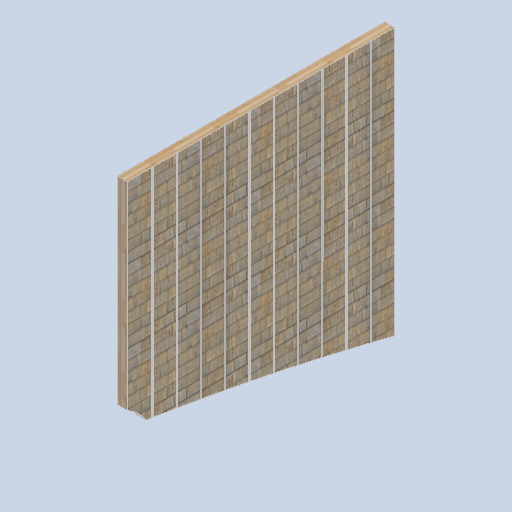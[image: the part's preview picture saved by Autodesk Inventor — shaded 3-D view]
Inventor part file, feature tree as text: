
AUTODESK INVENTOR PART (.ipt)
format: ipt  version: 2024.2 (Build 282272000, 272)  size: 508,928 bytes
history: native  units: mm
features: extrude x2, sketch x2
ambient origin geometry x8: Origin, YZ Plane, XZ Plane, XY Plane, X Axis, Y Axis, Z Axis, Center Point
bodies: Solid1 (feature_tree)
feature tree (4):
  extrude  "Extrusion1"  Depth=350.0mm
  extrude  "Extrusion2"  Depth=20.0mm
  sketch  "Sketch1"  dims[d0=150.0mm d1=0.0mm d2=350.0mm]
  sketch  "Sketch2"  dims[d3=10.0mm d4=20.0mm d5=350.0mm d6=20.0mm d7=350.0mm d8=10.0mm d9=20.0mm d10=350.0mm d11=20.0mm d12=350.0mm d13=350.0mm d14=10.0mm d15=20.0mm d16=350.0mm d17=20.0mm d18=350.0mm d19=20.0mm d20=350.0mm d21=20.0mm d22=350.0mm d23=20.0mm d24=0.0mm d25=0.0mm]
